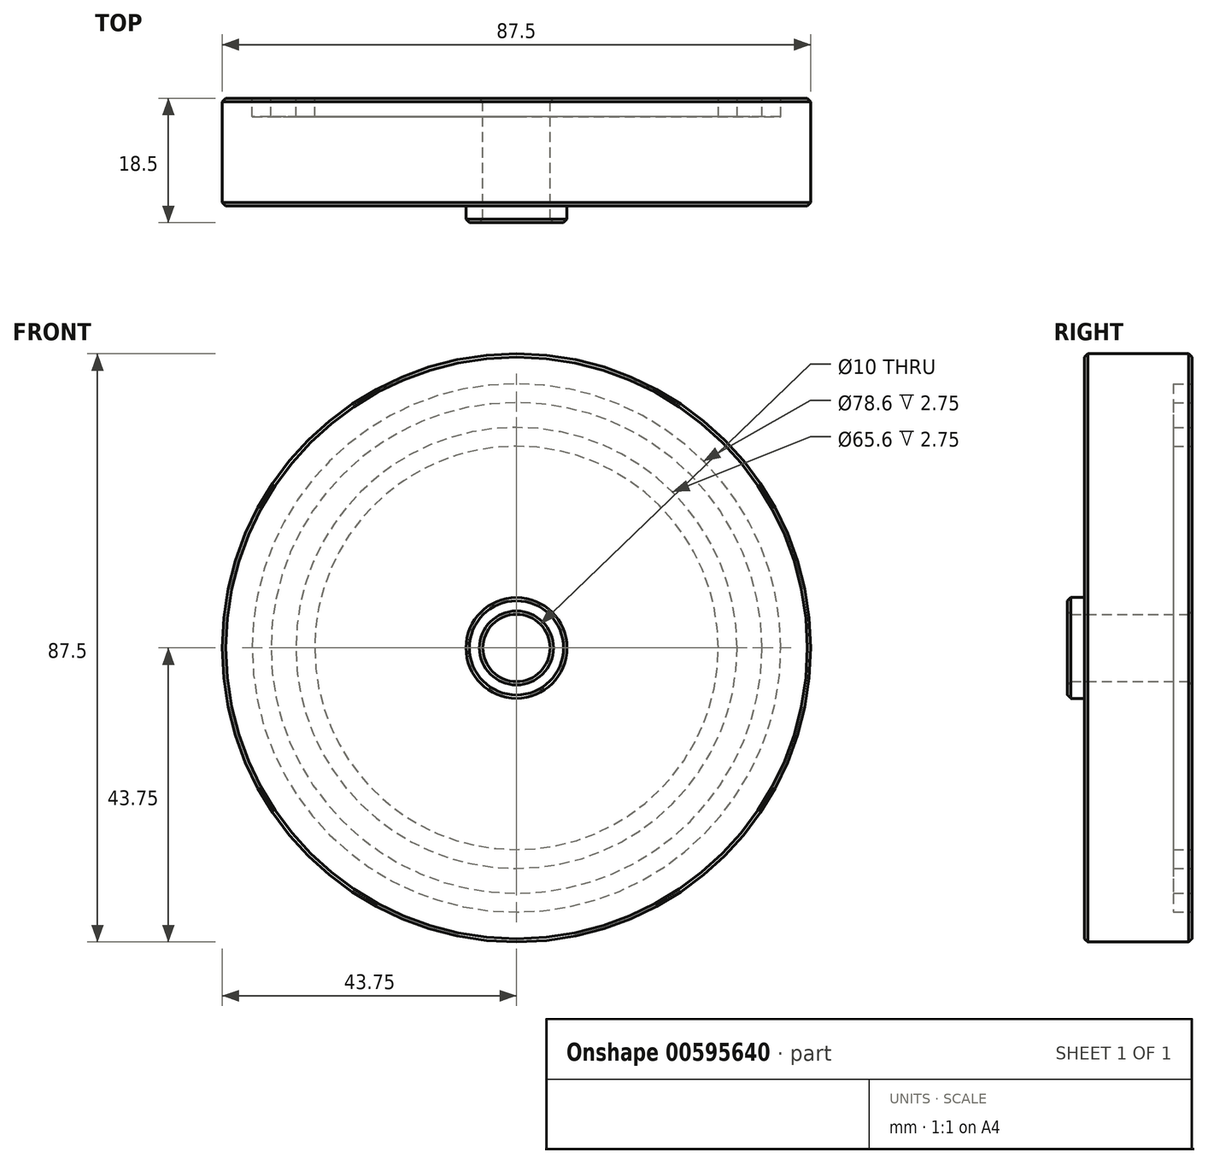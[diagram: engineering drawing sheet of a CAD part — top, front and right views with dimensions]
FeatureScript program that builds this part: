
annotation { "Feature Type Name" : "Feature", "Feature Type Description" : "" }
export const myFeature = defineFeature(function(context is Context, id is Id, definition is map)
    precondition{}
    {
        {
            var Q0;
            Q0=qCreatedBy(makeId("Front.planeOp"),FACE);
            var sketch = newSketch(context, id + "F0", { "sketchPlane" : qUnion([Q0])});
            skCircle(sketch, "E0", {"center": v(0, 0) * mm, "radius": 43.75 * mm});
            skCircle(sketch, "E1", {"center": v(0, 0) * mm, "radius": 5 * mm});
            skSolve(sketch);
        }
        {
            var Q0;
            Q0 = qSketchRegion(id + "F0", true);
            extrude(context, id + "F1", {"entities" : qUnion([Q0]), "depth" : 16 * mm, "offsetDistance" : 25 * mm});
        }
        {
            var Q0;
            Q0=makeQuery(id+"F1.opExtrude","CAP_FACE",FACE,{"disambiguationData":[OSD([sQuery(id+"F0.wireOp",EDGE,"E0"),sQuery(id+"F0.wireOp",EDGE,"E1")])],"isStart":false});
            var sketch = newSketch(context, id + "F2", { "sketchPlane" : qUnion([Q0])});
            skCircle(sketch, "E2", {"center": v(0, 0) * mm, "radius": 5 * mm});
            skCircle(sketch, "E3", {"center": v(0, 0) * mm, "radius": 7.5 * mm});
            skSolve(sketch);
        }
        {
            var Q0;
            Q0 = qSketchRegion(id + "F2", true);
            extrude(context, id + "F3", {"entities" : qUnion([Q0]), "operationType" : NewBodyOperationType.ADD, "depth" : 2.5 * mm, "offsetDistance" : 25 * mm});
        }
        {
            var Q0;
            Q0=makeQuery(id+"F1.opExtrude","CAP_FACE",FACE,{"disambiguationData":[OSD([sQuery(id+"F0.wireOp",EDGE,"E0"),sQuery(id+"F0.wireOp",EDGE,"E1")])],"isStart":true});
            var sketch = newSketch(context, id + "F4", { "sketchPlane" : qUnion([Q0])});
            skCircle(sketch, "E4", {"center": v(0, 0) * mm, "radius": 30 * mm});
            skCircle(sketch, "E5", {"center": v(0, 0) * mm, "radius": 36.5 * mm});
            skCircle(sketch, "E6", {"center": v(0, 0) * mm, "radius": 39.3 * mm});
            skCircle(sketch, "E7", {"center": v(0, 0) * mm, "radius": 32.8 * mm});
            skSolve(sketch);
        }
        {
            var Q0;
            Q0 = qSketchRegion(id + "F4", true);
            var Q1;
            Q1=makeQuery(id+"F4.imprint","IMPRINT",FACE,{"disambiguationData":[TD([[makeQuery(id+"F4.imprint","IMPRINT",EDGE,{"derivedFrom":sQuery(id+"F4.wireOp",EDGE,"E4")}),-1.0]])]});
            extrude(context, id + "F5", {"entities" : qUnion([Q0, Q1]), "operationType" : NewBodyOperationType.REMOVE, "oppositeDirection" : true, "depth" : 2.75 * mm, "offsetDistance" : 25 * mm});
        }
        {
            var Q0;
            Q0=makeQuery(id+"F3.opExtrude","CAP_EDGE",EDGE,{"disambiguationData":[OSD([sQuery(id+"F2.wireOp",EDGE,"E3")])],"isStart":false});
            var Q1;
            Q1=makeQuery(id+"F3.opExtrude","CAP_EDGE",EDGE,{"disambiguationData":[OSD([sQuery(id+"F2.wireOp",EDGE,"E2")])],"isStart":false});
            var Q2;
            Q2=makeQuery(id+"F1.opExtrude","CAP_EDGE",EDGE,{"disambiguationData":[OSD([sQuery(id+"F0.wireOp",EDGE,"E0")])],"isStart":false});
            var Q3;
            Q3=makeQuery(id+"F1.opExtrude","CAP_EDGE",EDGE,{"disambiguationData":[OSD([sQuery(id+"F0.wireOp",EDGE,"E0")])],"isStart":true});
            var Q4;
            Q4=makeQuery(id+"F1.opExtrude","CAP_EDGE",EDGE,{"disambiguationData":[OSD([sQuery(id+"F0.wireOp",EDGE,"E1")])],"isStart":true});
            chamfer(context, id + "F6", {"entities" : qUnion([Q0, Q1, Q2, Q3, Q4]), "width" : .5 * mm, "tangentPropagation" : true});
        }
    });
